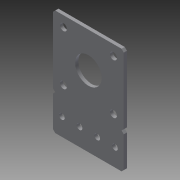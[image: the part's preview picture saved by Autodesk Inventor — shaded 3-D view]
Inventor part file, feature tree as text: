
AUTODESK INVENTOR PART (.ipt)
format: ipt  version: 2014 (Build 180170000, 170)  size: 155,136 bytes
history: native  units: in
note: dims shown in document units (in); Inventor stores cm internally (conversion verified against a paired STEP export)
features: other x1, extrude x1, imported_body x1, sketch x1
ambient origin geometry x8: Origin, YZ Plane, XZ Plane, XY Plane, X Axis, Y Axis, Z Axis, Center Point
bodies: Body1 (feature_tree)
feature tree (4):
  other  "Cut-Extrude1"
  extrude  "Extrusion2"  [1 undecoded]
  imported_body  "Base1"
  sketch  "Sketch2"  dims[d3=1.0in d4=0.0in]
note: 1 required parameter value undecoded (feature->parameter linkage not recoverable at this tier; creation-order binding heuristic only, values carry confidence <= 0.55)
